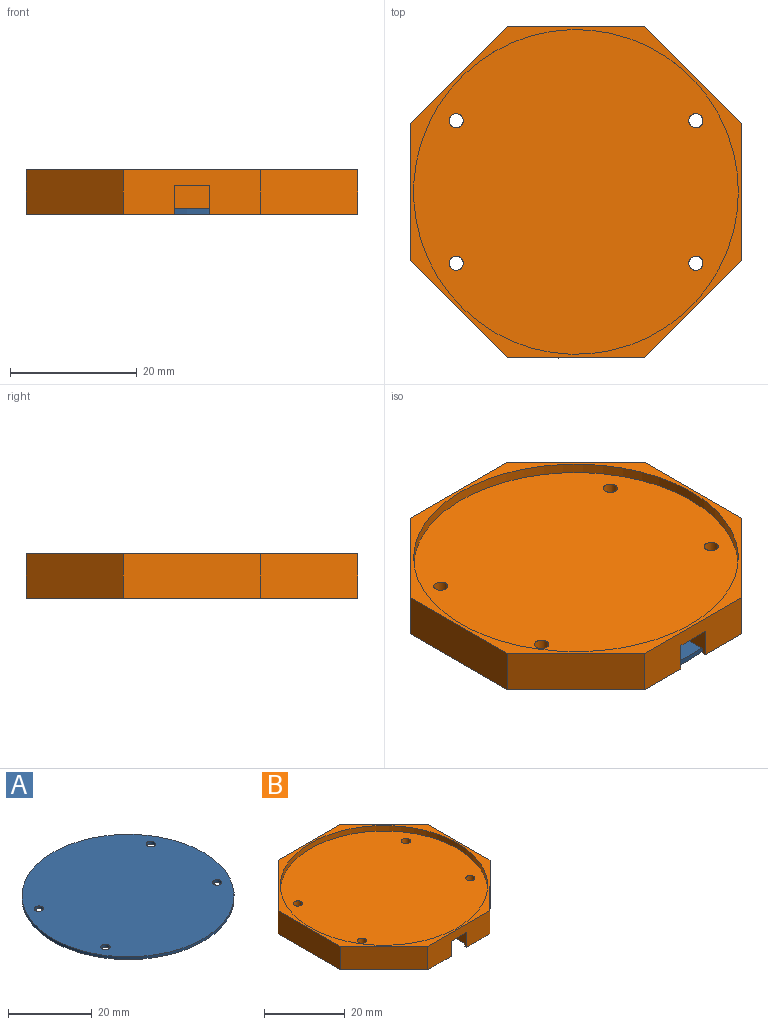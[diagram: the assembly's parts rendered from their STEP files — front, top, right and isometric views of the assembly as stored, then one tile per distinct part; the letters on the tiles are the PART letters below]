
ASSEMBLY  parts=2 mates=1
PART A: 7 faces, bbox 50.8x50.8x0.8 mm
  f0: cylinder r=25.4mm len=50.8mm, axis (0,0,-1), area 130.9mm2, adj f1,f2
  f1: plane 50.8x50.8mm, normal (0,0,1), area 2010.9mm2, adj f0,f3,f4,f5,f6
  f2: plane 50.8x50.8mm, normal (0,0,-1), area 2010.9mm2, adj f0,f3,f4,f5,f6
  f3: cylinder r=1.12mm len=2.25mm, axis (0,0,-1), area 5.8mm2, adj f1,f2
  f4: cylinder r=1.12mm len=2.25mm, axis (0,0,-1), area 5.8mm2, adj f1,f2
  f5: cylinder r=1.12mm len=2.25mm, axis (0,0,-1), area 5.8mm2, adj f1,f2
  f6: cylinder r=1.12mm len=2.25mm, axis (0,0,-1), area 5.8mm2, adj f1,f2
PART B: 26 faces, bbox 52.4x52.4x7 mm
  f0: plane 51.3x51.15mm, normal (0,0,-1), area 1654.6mm2, adj f12,f13,f14,f15,f17,f18,f19,f20
  f1: plane 41.5x11.1mm, normal (0,0,-1), area 399.8mm2, adj f3,f17,f18,f19,f20,f21,f22,f23
  f2: plane 15.36x15.36mm, normal (-0.71,-0.71,0), area 152mm2, adj f3,f9,f11,f25
  f3: plane 21.72x7mm, normal (0,-1,0), area 126.8mm2, adj f1,f2,f4,f11,f17,f23,f25
  f4: plane 15.36x15.36mm, normal (0.71,-0.71,0), area 152mm2, adj f3,f5,f11,f25
  f5: plane 21.72x7mm, normal (1,0,0), area 152mm2, adj f4,f6,f11,f25
  f6: plane 15.36x15.36mm, normal (0.71,0.71,0), area 152mm2, adj f5,f7,f11,f25
  f7: plane 21.72x7mm, normal (0,1,0), area 152mm2, adj f6,f8,f11,f25
  f8: plane 15.36x15.36mm, normal (-0.71,0.71,0), area 152mm2, adj f7,f9,f11,f25
  f9: plane 21.72x7mm, normal (-1,0,0), area 152mm2, adj f2,f8,f11,f25
  f10: cylinder r=25.65mm len=51.3mm, axis (0,0,-1), area 262.7mm2, adj f11,f16
  f11: plane 52.43x52.43mm, normal (0,0,1), area 210.3mm2, adj f2,f3,f4,f5,f6,f7,f8,f9
  f12: cylinder r=1.12mm len=4.55mm, axis (0,0,-1), area 32.2mm2, adj f0,f16
  f13: cylinder r=1.12mm len=4.55mm, axis (0,0,-1), area 32.2mm2, adj f0,f16
  f14: cylinder r=1.12mm len=4.55mm, axis (0,0,-1), area 32.2mm2, adj f0,f16
  f15: cylinder r=1.12mm len=4.55mm, axis (0,0,-1), area 32.2mm2, adj f0,f16
  f16: plane 51.3x51.3mm, normal (0,0,1), area 2051mm2, adj f10,f12,f13,f14,f15
  f17: plane 10.94x4.55mm, normal (1,0,0), area 41.4mm2, adj f0,f1,f3,f18,f24,f25
  f18: plane 3.73x2.78mm, normal (0,1,0), area 10.4mm2, adj f0,f1,f17,f19
  f19: plane 30.56x3.73mm, normal (1,0,0), area 114mm2, adj f0,f1,f18,f20
  f20: plane 11.1x3.73mm, normal (0,-1,0), area 41.4mm2, adj f0,f1,f19,f21
  f21: plane 30.56x3.73mm, normal (-1,0,0), area 114mm2, adj f0,f1,f20,f22
  f22: plane 3.73x2.78mm, normal (0,1,0), area 10.4mm2, adj f0,f1,f21,f23
  f23: plane 10.94x4.55mm, normal (-1,0,0), area 41.4mm2, adj f0,f1,f3,f22,f24,f25
  f24: cylinder r=25.65mm len=51.3mm, axis (0,0,1), area 127.6mm2, adj f0,f17,f23,f25
  f25: plane 52.43x52.43mm, normal (0,0,-1), area 206.9mm2, adj f2,f3,f4,f5,f6,f7,f8,f9
PLACE A t=(4.36,-48.08,-6.78)mm
PLACE B t=(53.26,-4.09,-2.23)mm
MATE fastened A.f5 <-> B.f15  axis (0,0,1) through (72.2,7.16,-5.96)mm
